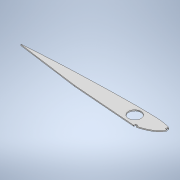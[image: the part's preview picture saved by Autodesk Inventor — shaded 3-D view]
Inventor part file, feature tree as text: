
AUTODESK INVENTOR PART (.ipt)
format: ipt  version: 2022 (Build 260153000, 153)  size: 168,960 bytes
history: native  units: mm
features: extrude x1, sketch x1
ambient origin geometry x8: Origin, YZ Plane, XZ Plane, XY Plane, X Axis, Y Axis, Z Axis, Center Point
bodies: Body1 (feature_tree)
feature tree (2):
  extrude  "Extrusion4"  Depth=160.0mm
  sketch  "Sketch1"  dims[d5=160.0mm d8=160.0mm d17=5.0mm d18=5.0mm d25=6.0mm d26=5.0mm d27=5.0mm d31=34.456mm d36=5.0mm d37=5.0mm d50=368.759386mm d62=31.0mm d63=2.5mm d64=0.0mm]
